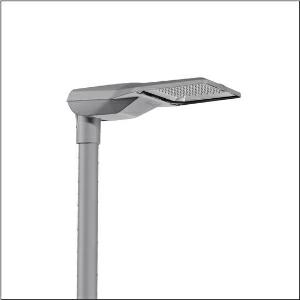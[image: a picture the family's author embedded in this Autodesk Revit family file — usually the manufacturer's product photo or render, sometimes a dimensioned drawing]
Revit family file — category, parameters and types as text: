
# Revit family: streetlight_sl_21_midi___pl52_5xe7h43a08mb_148e
name_source: partatom
category: Lighting Fixtures
units: mm (PartAtom-declared; Revit-internal decimal feet)

## family parameters
Cut with Voids When Loaded = No
Host = Face
Light Source = No
Part Type = Normal
Room Calculation Point = No
Round Connector Dimension = Use Diameter
Shared = No

## types (1)
- --- (1 x LED, 19830 lm, 147 W, 4000K)
    Apparent Load = 147 VA
    CIE Flux Codes = 27 59 98 100 100
    Color Rendering = 70
    Color Temperature = 4000K
    Default Elevation = 1800 mm
    Description = Streetlight SL 21 midi, mast luminaire, primary light control with lens, of PMMA, primary optical cover: cover, of toughened safety glass, transparent, light distribution: PL52, light emission: direct distribution, primary light characteristic: asymmetric, installation type: post-top, side-entry, LED, 3G 1.5mm², High Power LED, rated luminous flux: 19.830lm, luminous efficacy: 135lm/W, light colour: 740, colour temperature: 4000K, control: overheat protection, constant luminous flux control, time-dependent luminous flux control, flexible luminous flux parameterisation, mains connection: 220..240V, AC, 50/60Hz, connection cable pre-assembled, cable length: 12,5m, wiring characteristics: H07RN-F, start of lifetime: 147W, end of service life: 155W, reduction: 64W, luminaire housing, of diecast aluminium, powder-coated, Siteco® metallic grey (DB 702S), corrosivity category C5 mid according to DIN EN ISO 12944, please order mast flange separately, inclination adjustable: 0°, 5°, 10°, 15°, sealing non-destructively replaceable, multi-level sealing system, length: 644mm, width: 335mm, height: 110mm, mast flange for spigot size: 42mm (side-entry): 5XC10008XM4, 60/48mm (side-entry/post-top): 5XC10108XM2, 76/60mm (side-entry/post-top): 5XC10108XM1, protection rating (complete): IP66, insulation class (complete): insulation class II (safety insulation), certification: CE, ENEC, ENEC+, VDE, impact resistance: IK09, permissible operating ambient temperature for outdoor applications: -40..+50°C, standard-compliant lighting for roads and squares, packaging unit: 1 piece

Light Distribution: PL52
    Height = 111 mm
    Lamp = 1 x LED
    Lamp Light Flux = 19830 lm
    Lamp Power = 147 W
    Lamp count = 1
    Length = 644 mm
    Luminous efficacy = 135 lm/W
    Manufacturer = Siteco
    ModVariant = No
    Model = 5XE7H43A08MB
    Number of Poles = 1
    OnlyDefault = Yes
    Power Factor = 1
    Product Name = Streetlight SL 21 midi | PL52
    Product group = mast luminaire | pylon top
    ProductGroupID = 6100
    Protection Class = Protection class II
    Protection Degree = IP 66
    RLX_Detail_Level = 1
    RLX_Emergency_Light_Flux = 0 lm
    RLX_Emergency_Type = 0
    RLX_Emergency_Type_DB = No
    RlxData = <blob elided: 100569 chars, md5=d06b2150>
    Socket = socket
    Standby Power = 0 W
    System Light Flux = 19830 lm
    System Power = 147 W
    Type Comments = factory setting: luminous flux: 100 % | Output Level: 100 % | 750 mA
    Type Image = l_1004298.jpg
    URL = http://relux.com
    VarID = @adj_142719
    Voltage = 0 V
    Weight = 0.00 kg
    Width = 336 mm

## geometry (parser evidence)
native form markers: Blend x4, Sweep x9
no freeform markers — native parametric forms only
